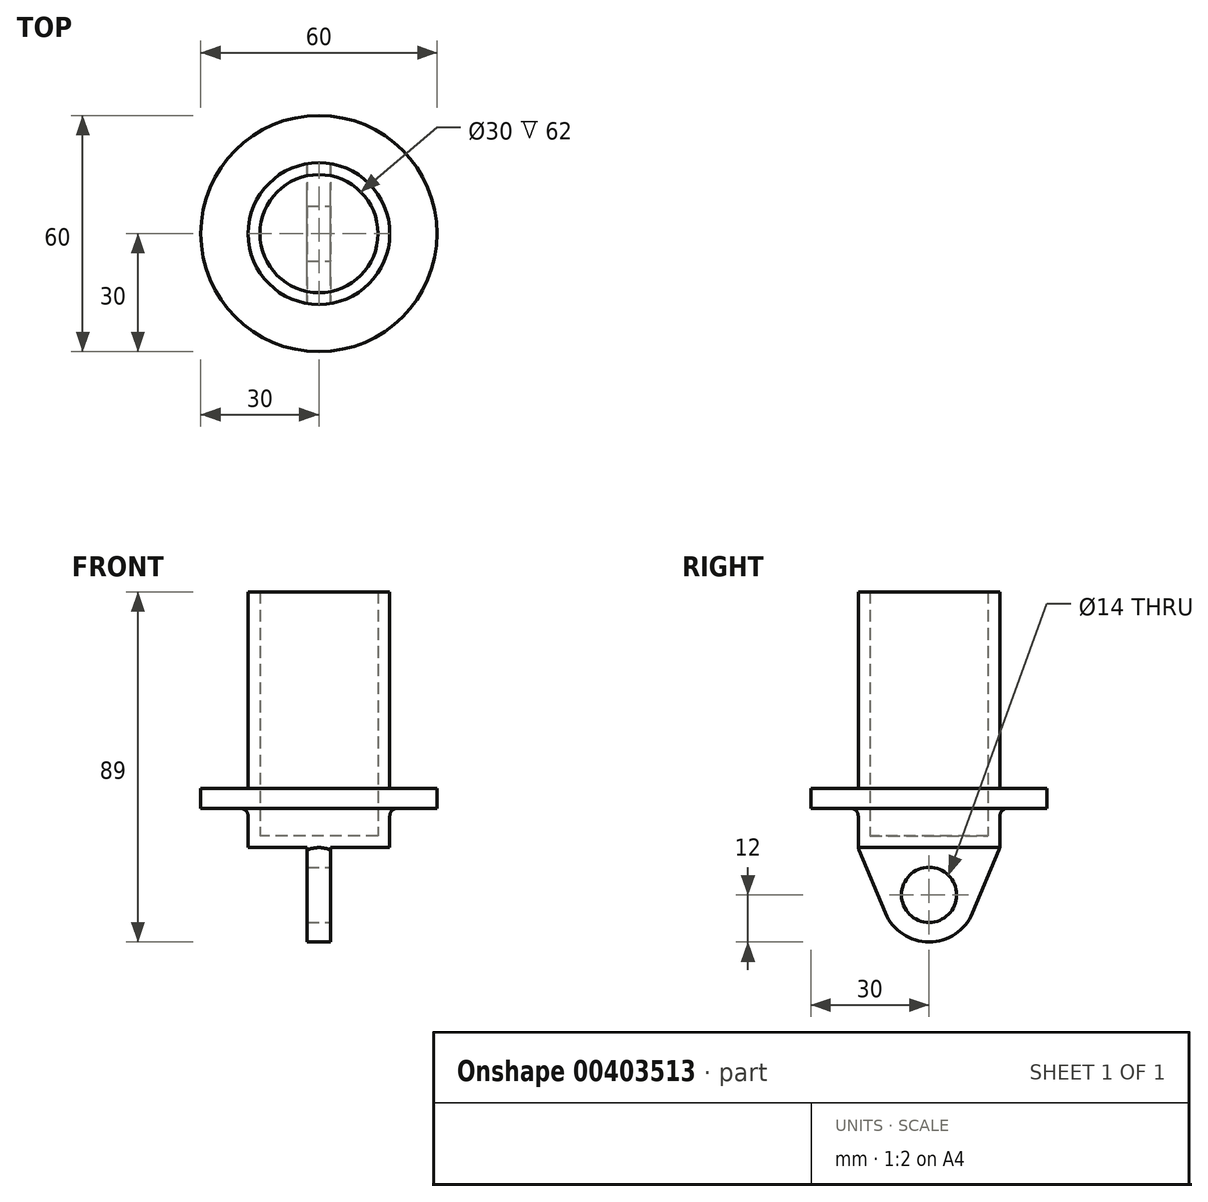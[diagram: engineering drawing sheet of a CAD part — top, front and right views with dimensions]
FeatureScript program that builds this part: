
annotation { "Feature Type Name" : "Feature", "Feature Type Description" : "" }
export const myFeature = defineFeature(function(context is Context, id is Id, definition is map)
    precondition{}
    {
        {
            var Q0;
            Q0=qCreatedBy(makeId("Top.planeOp"),FACE);
            var sketch = newSketch(context, id + "F0", { "sketchPlane" : qUnion([Q0])});
            skCircle(sketch, "E0", {"center": v(0, 0) * mm, "radius": 15 * mm, "construction": true});
            skCircle(sketch, "E1", {"center": v(0, 0) * mm, "radius": 18 * mm});
            skSolve(sketch);
        }
        {
            var Q0;
            Q0 = qSketchRegion(id + "F0", true);
            extrude(context, id + "F1", {"entities" : qUnion([Q0]), "depth" : 65 * mm});
        }
        {
            var Q0;
            Q0=makeQuery(id+"F1.opExtrude","CAP_FACE",FACE,{"disambiguationData":[OSD([sQuery(id+"F0.wireOp",EDGE,"E1")])],"isStart":false});
            shell(context, id + "F2", {"entities" : qUnion([Q0]), "thickness" : 3 * mm});
        }
        {
            var Q0;
            Q0=makeQuery(id+"F1.opExtrude","CAP_FACE",FACE,{"disambiguationData":[OSD([sQuery(id+"F0.wireOp",EDGE,"E1")])],"isStart":true});
            var sketch = newSketch(context, id + "F3", { "sketchPlane" : qUnion([Q0])});
            skArc(sketch, "E2", {"start": v(-3, -17.75) * mm, "mid": v(0, -18) * mm, "end": v(3, -17.75) * mm, "construction": true});
            skLineSegment(sketch, "E3", {"start": v(-3, 17.75) * mm, "end": v(-3, -17.75) * mm});
            skLineSegment(sketch, "E4.MirrorCS", {"start": v(3, 17.75) * mm, "end": v(3, -17.75) * mm});
            skArc(sketch, "E5", {"start": v(3, 17.75) * mm, "mid": v(0, 18) * mm, "end": v(-3, 17.75) * mm});
            skArc(sketch, "E6.trimOffspring", {"start": v(3, 17.75) * mm, "mid": v(0, 18) * mm, "end": v(-3, 17.75) * mm, "construction": true});
            skArc(sketch, "E7.trimOffspring", {"start": v(-3, -17.75) * mm, "mid": v(0, -18) * mm, "end": v(3, -17.75) * mm});
            skSolve(sketch);
        }
        {
            var Q0;
            Q0 = qSketchRegion(id + "F3", true);
            extrude(context, id + "F4", {"entities" : qUnion([Q0]), "operationType" : NewBodyOperationType.ADD, "depth" : 30 * mm});
        }
        {
            var Q0;
            Q0=makeQuery(id+"F4.opExtrude","SWEPT_FACE",FACE,{"disambiguationData":[OSD([sQuery(id+"F3.wireOp",EDGE,"E4.MirrorCS")])]});
            var sketch = newSketch(context, id + "F5", { "sketchPlane" : qUnion([Q0])});
            skCircle(sketch, "E8", {"center": v(0, -12) * mm, "radius": 7 * mm});
            skSolve(sketch);
        }
        {
            var Q0;
            Q0=makeQuery(id+"F5.imprint","IMPRINT",FACE,{"disambiguationData":[TD([[makeQuery(id+"F5.imprint","IMPRINT",EDGE,{"derivedFrom":sQuery(id+"F5.wireOp",EDGE,"E8")}),1.0]])]});
            extrude(context, id + "F6", {"entities" : qUnion([Q0]), "operationType" : NewBodyOperationType.REMOVE, "oppositeDirection" : true, "depth" : 25 * mm});
        }
        {
            var Q0;
            Q0=makeQuery(id+"F4.opExtrude","SWEPT_FACE",FACE,{"disambiguationData":[OSD([sQuery(id+"F3.wireOp",EDGE,"E4.MirrorCS")])]});
            var sketch = newSketch(context, id + "F7", { "sketchPlane" : qUnion([Q0])});
            skCircle(sketch, "E9", {"center": v(0, -12) * mm, "radius": 12 * mm, "construction": true});
            skLineSegment(sketch, "E10", {"start": v(0, -12) * mm, "end": v(-12, -12) * mm, "construction": true});
            skLineSegment(sketch, "E11", {"start": v(0, -12) * mm, "end": v(12, -12) * mm, "construction": true});
            skLineSegment(sketch, "E12", {"start": v(-18, -30) * mm, "end": v(-18, 40) * mm, "construction": true});
            skLineSegment(sketch, "E13", {"start": v(18, 40) * mm, "end": v(18, -30) * mm, "construction": true});
            skLineSegment(sketch, "E14", {"start": v(-18, 0) * mm, "end": v(-11.08, -16.62) * mm, "construction": true});
            skLineSegment(sketch, "E15.MirrorCS", {"start": v(18, 0) * mm, "end": v(11.08, -16.62) * mm, "construction": true});
            skLineSegment(sketch, "E16", {"start": v(-18, -30) * mm, "end": v(18, -30) * mm});
            skLineSegment(sketch, "E17", {"start": v(18, 0) * mm, "end": v(18, -30) * mm});
            skLineSegment(sketch, "E18", {"start": v(18, 0) * mm, "end": v(11.08, -16.62) * mm});
            skLineSegment(sketch, "E19", {"start": v(-11.08, -16.62) * mm, "end": v(-18, 0) * mm});
            skLineSegment(sketch, "E20", {"start": v(-18, -30) * mm, "end": v(-18, 0) * mm});
            skArc(sketch, "E21", {"start": v(-11.08, -16.62) * mm, "mid": v(0, -24) * mm, "end": v(11.08, -16.62) * mm});
            skSolve(sketch);
        }
        {
            var Q0;
            Q0 = qSketchRegion(id + "F7", true);
            extrude(context, id + "F8", {"entities" : qUnion([Q0]), "operationType" : NewBodyOperationType.REMOVE, "endBound" : BoundingType.THROUGH_ALL, "oppositeDirection" : true, "depth" : 25 * mm});
        }
        {
            var Q0;
            Q0=qCreatedBy(makeId("Top.planeOp"),FACE);
            cPlane(context, id + "F9", {"entities" : qUnion([Q0]), "cplaneType" : CPlaneType.OFFSET, "offset" : 10 * mm, "width" : 150 * mm, "height" : 150 * mm});
        }
        {
            var Q0;
            Q0=qCreatedBy(id+"F9.planeOp",FACE);
            var sketch = newSketch(context, id + "F10", { "sketchPlane" : qUnion([Q0])});
            skCircle(sketch, "E22", {"center": v(0, 0) * mm, "radius": 18 * mm});
            skCircle(sketch, "E23", {"center": v(0, 0) * mm, "radius": 30 * mm});
            skSolve(sketch);
        }
        {
            var Q0;
            Q0=makeQuery(id+"F10.imprint","IMPRINT",FACE,{"disambiguationData":[TD([[makeQuery(id+"F10.imprint","IMPRINT",EDGE,{"derivedFrom":sQuery(id+"F10.wireOp",EDGE,"E22")}),-1.0]])]});
            extrude(context, id + "F11", {"entities" : qUnion([Q0]), "operationType" : NewBodyOperationType.ADD, "depth" : 5 * mm});
        }
        {
            var Q0;
            Q0=makeQuery(id+"F11.opExtrude","CAP_EDGE",EDGE,{"disambiguationData":[OSD([sQuery(id+"F10.wireOp",EDGE,"E22")])],"isStart":false});
            var Q1;
            Q1=makeQuery(id+"F11.opExtrude","CAP_EDGE",EDGE,{"disambiguationData":[OSD([sQuery(id+"F10.wireOp",EDGE,"E22")])],"isStart":true});
            fillet(context, id + "F12", {"entities" : qUnion([Q0, Q1]), "radius" : 2 * mm, "tangentPropagation" : true, "allowEdgeOverflow" : false});
        }
    });
